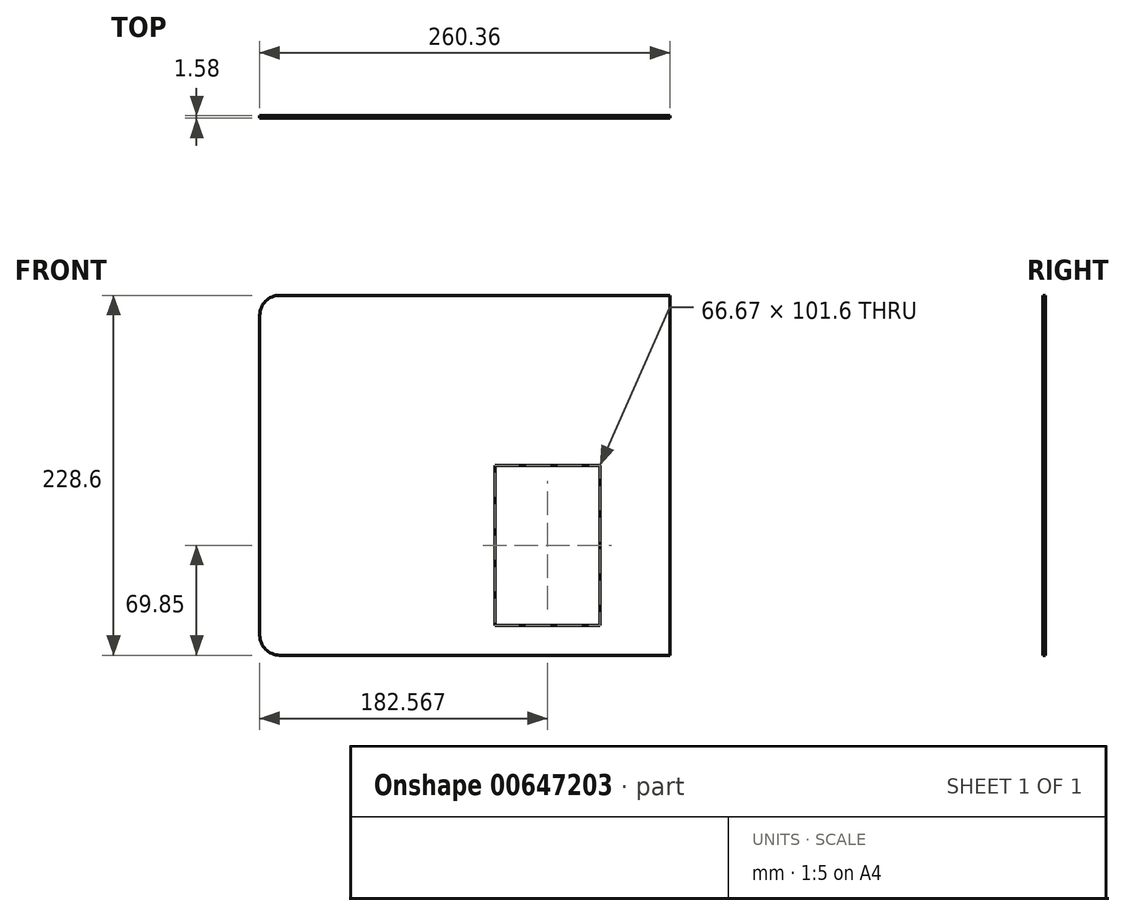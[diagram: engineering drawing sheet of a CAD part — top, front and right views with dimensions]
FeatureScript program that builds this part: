
annotation { "Feature Type Name" : "Feature", "Feature Type Description" : "" }
export const myFeature = defineFeature(function(context is Context, id is Id, definition is map)
    precondition{}
    {
        {
            var Q0;
            Q0=qCreatedBy(makeId("Front.planeOp"),FACE);
            var sketch = newSketch(context, id + "F0", { "sketchPlane" : qUnion([Q0])});
            skLineSegment(sketch, "E0.bottom", {"start": v(-117.48, 114.3) * mm, "end": v(117.47, 114.3) * mm});
            skLineSegment(sketch, "E0.top", {"start": v(-117.48, -114.3) * mm, "end": v(117.47, -114.3) * mm});
            skLineSegment(sketch, "E0.left", {"start": v(-130.18, 101.6) * mm, "end": v(-130.18, -101.6) * mm});
            skLineSegment(sketch, "E0.right", {"start": v(130.18, 101.6) * mm, "end": v(130.18, -101.6) * mm});
            skPoint(sketch, "E0.middle", {"position": v(0, 0) * mm});
            skLineSegment(sketch, "E1.bottom", {"start": v(85.72, -95.25) * mm, "end": v(19.05, -95.25) * mm});
            skLineSegment(sketch, "E1.top", {"start": v(85.72, 6.35) * mm, "end": v(19.05, 6.35) * mm});
            skLineSegment(sketch, "E1.left", {"start": v(85.72, -95.25) * mm, "end": v(85.72, 6.35) * mm});
            skLineSegment(sketch, "E1.right", {"start": v(19.05, -95.25) * mm, "end": v(19.05, 6.35) * mm});
            skPoint(sketch, "E2.visualSharp", {"position": v(-130.18, 114.3) * mm});
            skArc(sketch, "E2.filletArc", {"start": v(-117.48, 114.3) * mm, "mid": v(-126.46, 110.58) * mm, "end": v(-130.18, 101.6) * mm});
            skPoint(sketch, "E3.visualSharp", {"position": v(130.18, 114.3) * mm});
            skPoint(sketch, "E4.visualSharp", {"position": v(-130.18, -114.3) * mm});
            skArc(sketch, "E4.filletArc", {"start": v(-130.18, -101.6) * mm, "mid": v(-126.46, -110.58) * mm, "end": v(-117.48, -114.3) * mm});
            skPoint(sketch, "E5.visualSharp", {"position": v(130.18, -114.3) * mm});
            skLineSegment(sketch, "E6", {"start": v(117.47, 114.3) * mm, "end": v(130.18, 114.3) * mm});
            skLineSegment(sketch, "E7", {"start": v(130.18, 101.6) * mm, "end": v(130.18, 114.3) * mm});
            skLineSegment(sketch, "E8", {"start": v(130.18, -101.6) * mm, "end": v(130.18, -114.3) * mm});
            skLineSegment(sketch, "E9", {"start": v(130.18, -114.3) * mm, "end": v(117.47, -114.3) * mm});
            skSolve(sketch);
        }
        {
            var Q0;
            Q0=makeQuery(id+"F0.imprint","IMPRINT",FACE,{"disambiguationData":[TD([[makeQuery(id+"F0.imprint","IMPRINT",EDGE,{"derivedFrom":sQuery(id+"F0.wireOp",EDGE,"E0.bottom")}),-1.0]])]});
            extrude(context, id + "F1", {"entities" : qUnion([Q0]), "endBound" : BoundingType.SYMMETRIC, "depth" : 1.59 * mm, "offsetDistance" : 25.4 * mm});
        }
    });
